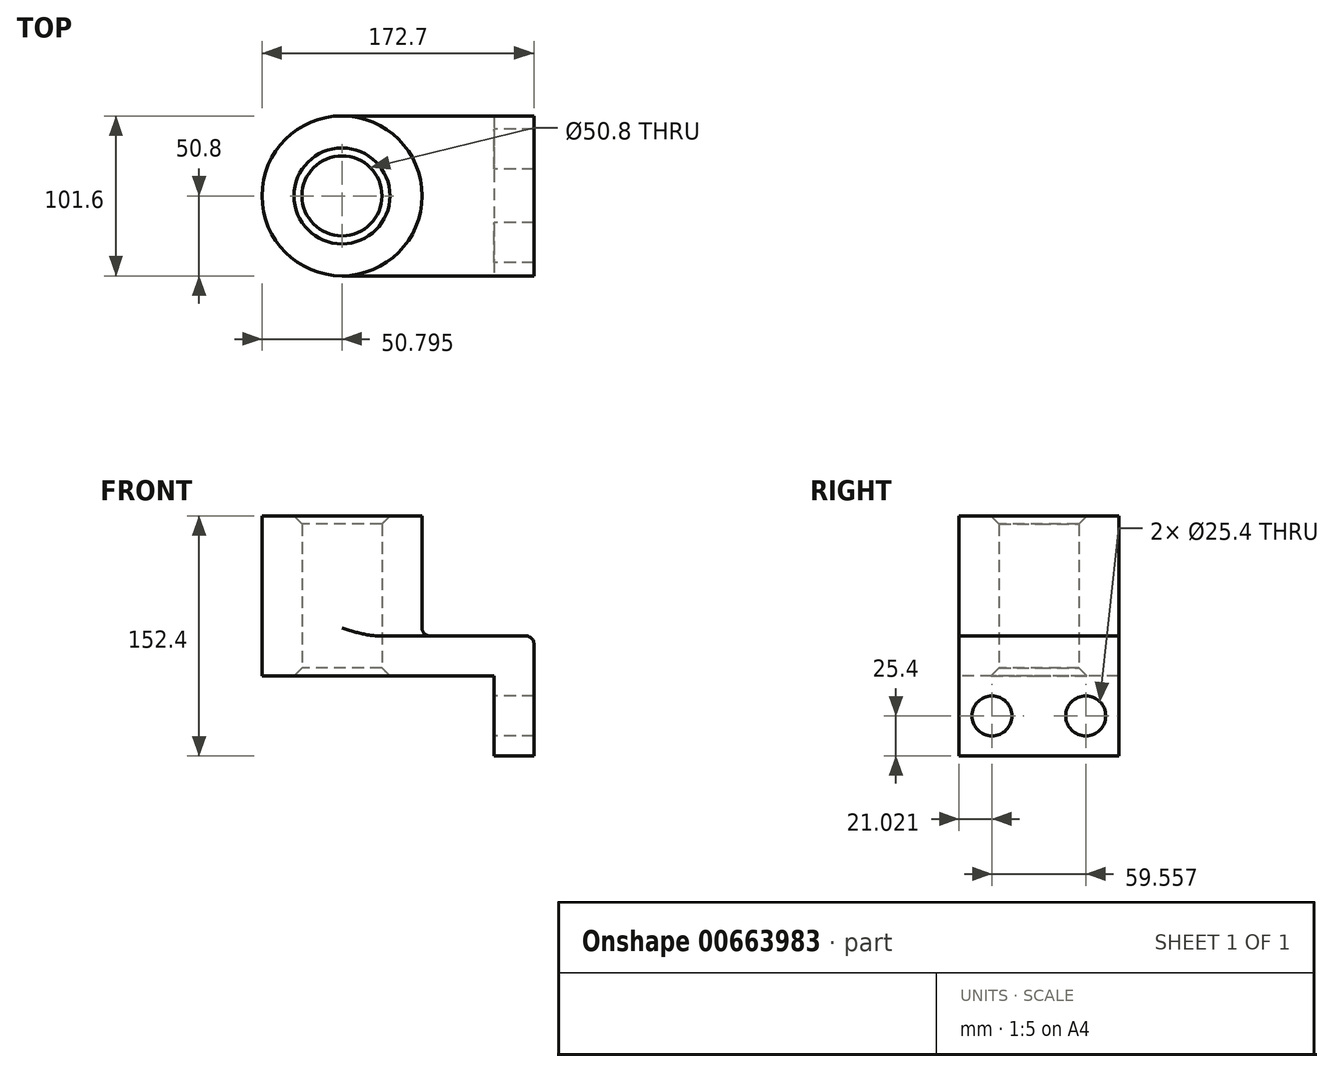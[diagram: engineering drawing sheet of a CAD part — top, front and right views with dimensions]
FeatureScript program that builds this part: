
annotation { "Feature Type Name" : "Feature", "Feature Type Description" : "" }
export const myFeature = defineFeature(function(context is Context, id is Id, definition is map)
    precondition{}
    {
        {
            var Q0;
            Q0=qCreatedBy(makeId("Top.planeOp"),FACE);
            var sketch = newSketch(context, id + "F0", { "sketchPlane" : qUnion([Q0])});
            skLineSegment(sketch, "E0.bottom", {"start": v(-48.25, 50.8) * mm, "end": v(48.25, 50.8) * mm});
            skLineSegment(sketch, "E0.top", {"start": v(-48.25, -50.8) * mm, "end": v(48.25, -50.8) * mm});
            skLineSegment(sketch, "E0.left", {"start": v(-48.25, 50.8) * mm, "end": v(-48.25, -50.8) * mm});
            skLineSegment(sketch, "E0.right", {"start": v(48.25, 50.8) * mm, "end": v(48.25, -50.8) * mm});
            skPoint(sketch, "E0.middle", {"position": v(0, 0) * mm});
            skCircle(sketch, "E1", {"center": v(-48.25, 0) * mm, "radius": 50.8 * mm});
            skCircle(sketch, "E2", {"center": v(-48.25, 0) * mm, "radius": 25.4 * mm});
            skSolve(sketch);
        }
        {
            var Q0;
            Q0 = qSketchRegion(id + "F0", true);
            extrude(context, id + "F1", {"entities" : qUnion([Q0]), "depth" : 25.4 * mm, "offsetDistance" : 25.4 * mm});
        }
        {
            var Q0;
            {var subQ1=sQuery(id+"F0.wireOp",EDGE,"E0.left");var subQ3=sQuery(id+"F0.wireOp",EDGE,"E2");var subQ4=makeQuery(id+"F0.imprint","INTERSECT",VERTEX,{"disambiguationData":[OD(0.0)],"derivedFrom":[subQ1,subQ3]});Q0=makeQuery(id+"F0.imprint","IMPRINT",FACE,{"disambiguationData":[TD([[makeQuery(id+"F0.imprint","IMPRINT",EDGE,{"disambiguationData":[TD([[subQ4,1.0]])],"derivedFrom":subQ3}),-1.0]])]});}
            var Q1;
            {var subQ1=sQuery(id+"F0.wireOp",EDGE,"E0.left");var subQ3=sQuery(id+"F0.wireOp",EDGE,"E2");var subQ4=makeQuery(id+"F0.imprint","INTERSECT",VERTEX,{"disambiguationData":[OD(0.0)],"derivedFrom":[subQ1,subQ3]});Q1=makeQuery(id+"F0.imprint","IMPRINT",FACE,{"disambiguationData":[TD([[makeQuery(id+"F0.imprint","IMPRINT",EDGE,{"disambiguationData":[TD([[subQ4,-1.0]])],"derivedFrom":subQ3}),-1.0]])]});}
            extrude(context, id + "F2", {"entities" : qUnion([Q0, Q1]), "operationType" : NewBodyOperationType.ADD, "depth" : 101.6 * mm, "offsetDistance" : 25.4 * mm});
        }
        {
            var Q0;
            Q0=makeQuery(id+"F1.opExtrude","SWEPT_FACE",FACE,{"disambiguationData":[OSD([sQuery(id+"F0.wireOp",EDGE,"E0.right")])]});
            var sketch = newSketch(context, id + "F3", { "sketchPlane" : qUnion([Q0])});
            skLineSegment(sketch, "E3.bottom", {"start": v(-50.8, 25.4) * mm, "end": v(50.8, 25.4) * mm});
            skLineSegment(sketch, "E3.top", {"start": v(-50.8, -50.8) * mm, "end": v(50.8, -50.8) * mm});
            skLineSegment(sketch, "E3.left", {"start": v(-50.8, 25.4) * mm, "end": v(-50.8, -50.8) * mm});
            skLineSegment(sketch, "E3.right", {"start": v(50.8, 25.4) * mm, "end": v(50.8, -50.8) * mm});
            skCircle(sketch, "E4", {"center": v(-29.78, -25.4) * mm, "radius": 12.7 * mm});
            skLineSegment(sketch, "E5", {"start": v(0, 0) * mm, "end": v(0, -50.8) * mm, "construction": true});
            skCircle(sketch, "E6.MirrorC", {"center": v(29.78, -25.4) * mm, "radius": 12.7 * mm});
            skSolve(sketch);
        }
        {
            var Q0;
            Q0 = qSketchRegion(id + "F3", true);
            extrude(context, id + "F4", {"entities" : qUnion([Q0]), "operationType" : NewBodyOperationType.ADD, "depth" : 25.4 * mm, "offsetDistance" : 25.4 * mm});
        }
        {
            var Q0;
            {var subQ0=sQuery(id+"F0.wireOp",EDGE,"E1");Q0=makeQuery(id+"F2.boolean.opBoolean","INTERSECT",EDGE,{"derivedFrom":[makeQuery(id+"F1.opExtrude","CAP_FACE",FACE,{"disambiguationData":[OSD([sQuery(id+"F0.wireOp",EDGE,"E0.bottom"),sQuery(id+"F0.wireOp",EDGE,"E0.top"),sQuery(id+"F0.wireOp",EDGE,"E0.right"),subQ0,sQuery(id+"F0.wireOp",EDGE,"E2")])],"isStart":false}),makeQuery(id+"F2.opExtrude","SWEPT_FACE",FACE,{"disambiguationData":[OSD([subQ0])]})]});}
            fillet(context, id + "F5", {"entities" : qUnion([Q0]), "radius" : 5.08 * mm, "tangentPropagation" : true, "allowEdgeOverflow" : false});
        }
        {
            var Q0;
            Q0=makeQuery(id+"F4.opExtrude","CAP_EDGE",EDGE,{"disambiguationData":[OSD([sQuery(id+"F3.wireOp",EDGE,"E3.bottom")])],"isStart":false});
            fillet(context, id + "F6", {"entities" : qUnion([Q0]), "radius" : 5.08 * mm, "tangentPropagation" : true, "allowEdgeOverflow" : false});
        }
        {
            var Q0;
            {var subQ0=sQuery(id+"F0.wireOp",EDGE,"E2");Q0=makeQuery(id+"F2.boolean.opBoolean","MERGE",FACE,{"derivedFrom":[makeQuery(id+"F1.opExtrude","SWEPT_FACE",FACE,{"disambiguationData":[OSD([subQ0])]}),makeQuery(id+"F2.opExtrude","SWEPT_FACE",FACE,{"disambiguationData":[OSD([subQ0])]})]});}
            chamfer(context, id + "F7", {"entities" : qUnion([Q0]), "chamferType" : ChamferType.OFFSET_ANGLE, "width" : 5.08 * mm, "oppositeDirection" : false, "angle" : 45 * degree, "tangentPropagation" : true});
        }
    });
